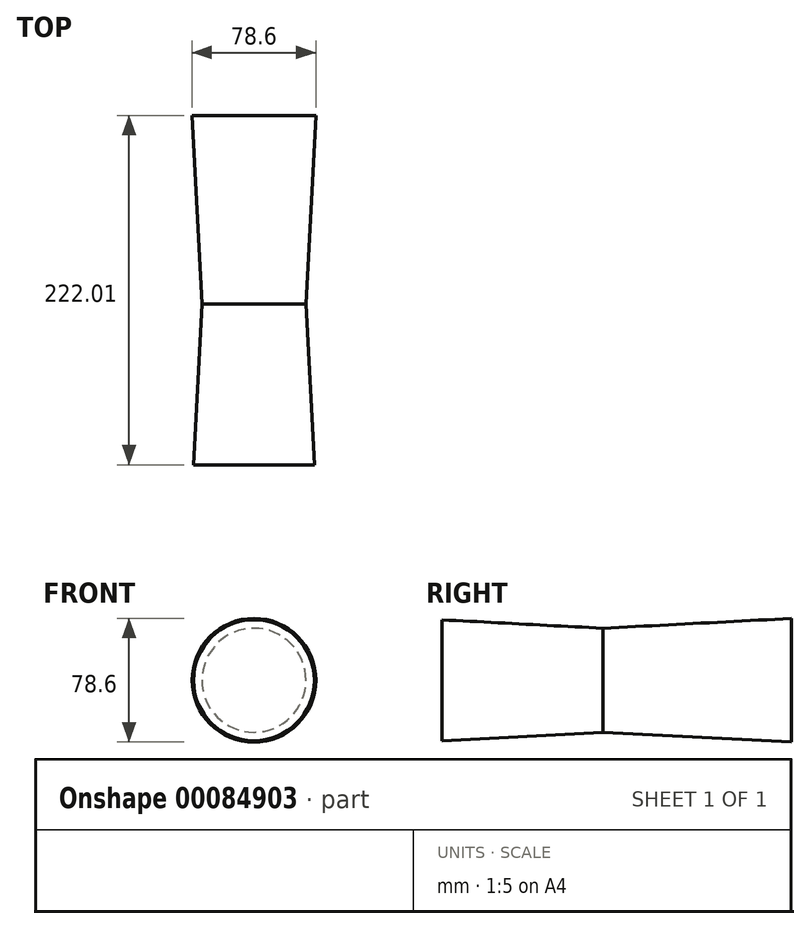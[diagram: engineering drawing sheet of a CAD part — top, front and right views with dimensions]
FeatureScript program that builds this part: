
annotation { "Feature Type Name" : "Feature", "Feature Type Description" : "" }
export const myFeature = defineFeature(function(context is Context, id is Id, definition is map)
    precondition{}
    {
        {
            var Q0;
            Q0=qCreatedBy(makeId("Front.planeOp"),FACE);
            var sketch = newSketch(context, id + "F0", { "sketchPlane" : qUnion([Q0])});
            skCircle(sketch, "E0", {"center": v(0, 0) * mm, "radius": 33.02 * mm});
            skSolve(sketch);
        }
        {
            var Q0;
            Q0=makeQuery(id+"F0.imprint","IMPRINT",FACE,{"disambiguationData":[TD([[makeQuery(id+"F0.imprint","IMPRINT",EDGE,{"derivedFrom":sQuery(id+"F0.wireOp",EDGE,"E0")}),1.0]])]});
            extrude(context, id + "F1", {"entities" : qUnion([Q0]), "oppositeDirection" : true, "depth" : 119.78 * mm, "hasDraft" : true, "draftAngle" : 3 * degree, "hasSecondDirection" : true, "secondDirectionOppositeDirection" : false, "secondDirectionDepth" : 102.23 * mm, "hasSecondDirectionDraft" : true, "secondDirectionDraftAngle" : 3 * degree});
        }
    });
